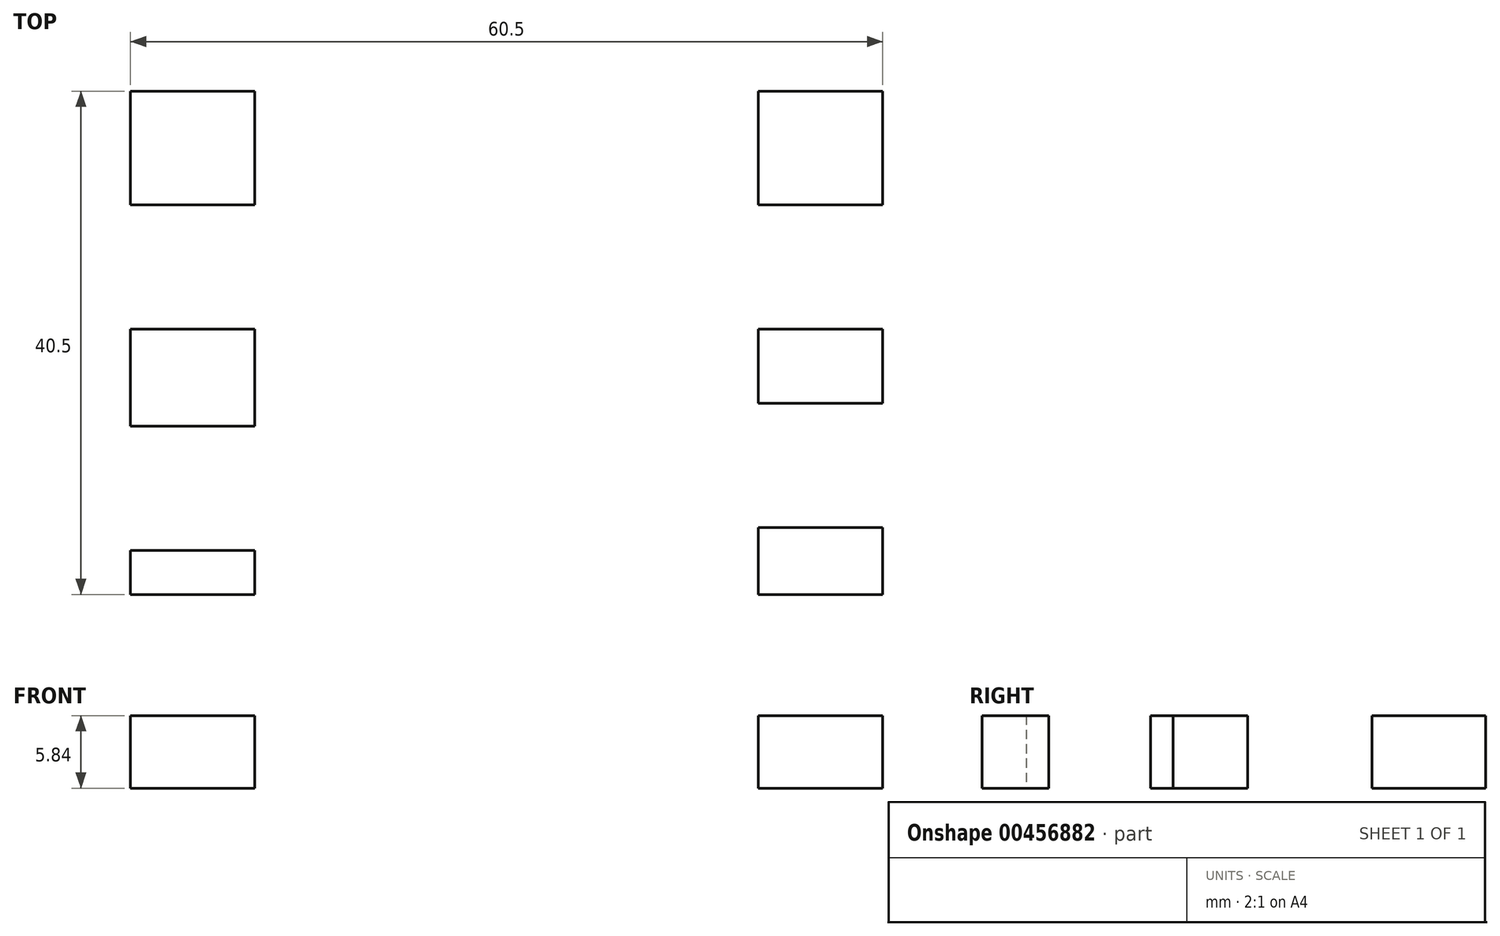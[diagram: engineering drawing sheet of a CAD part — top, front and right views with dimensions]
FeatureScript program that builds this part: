
annotation { "Feature Type Name" : "Feature", "Feature Type Description" : "" }
export const myFeature = defineFeature(function(context is Context, id is Id, definition is map)
    precondition{}
    {
        {
            var Q0;
            Q0=qCreatedBy(makeId("Top.planeOp"),FACE);
            var sketch = newSketch(context, id + "F0", { "sketchPlane" : qUnion([Q0])});
            skLineSegment(sketch, "E0.bottom", {"start": v(-20.25, 20.25) * mm, "end": v(20.25, 20.25) * mm});
            skLineSegment(sketch, "E0.top", {"start": v(-20.25, -20.25) * mm, "end": v(20.25, -20.25) * mm});
            skLineSegment(sketch, "E0.left", {"start": v(-20.25, 20.25) * mm, "end": v(-20.25, -20.25) * mm});
            skLineSegment(sketch, "E0.right", {"start": v(20.25, 20.25) * mm, "end": v(20.25, -20.25) * mm});
            skPoint(sketch, "E1", {"position": v(-20.25, 20.25) * mm});
            skPoint(sketch, "E2", {"position": v(0, 20.25) * mm});
            skPoint(sketch, "E3", {"position": v(20.25, 20.25) * mm});
            skLineSegment(sketch, "E4.bottom", {"start": v(-20.25, 11.12) * mm, "end": v(-30.25, 11.12) * mm});
            skLineSegment(sketch, "E4.top", {"start": v(-20.25, 1.12) * mm, "end": v(-30.25, 1.12) * mm});
            skLineSegment(sketch, "E4.left", {"start": v(-20.25, 11.12) * mm, "end": v(-20.25, 1.12) * mm});
            skLineSegment(sketch, "E4.right", {"start": v(-30.25, 11.12) * mm, "end": v(-30.25, 1.12) * mm});
            skLineSegment(sketch, "E5.bottom", {"start": v(-20.25, -6.7) * mm, "end": v(-30.25, -6.7) * mm});
            skLineSegment(sketch, "E5.top", {"start": v(-20.25, -16.7) * mm, "end": v(-30.25, -16.7) * mm});
            skLineSegment(sketch, "E5.left", {"start": v(-20.25, -6.7) * mm, "end": v(-20.25, -16.7) * mm});
            skLineSegment(sketch, "E5.right", {"start": v(-30.25, -6.7) * mm, "end": v(-30.25, -16.7) * mm});
            skLineSegment(sketch, "E6.bottom", {"start": v(20.25, 11.12) * mm, "end": v(30.25, 11.12) * mm});
            skLineSegment(sketch, "E6.top", {"start": v(20.25, 1.12) * mm, "end": v(30.25, 1.12) * mm});
            skLineSegment(sketch, "E6.left", {"start": v(20.25, 11.12) * mm, "end": v(20.25, 1.12) * mm});
            skLineSegment(sketch, "E6.right", {"start": v(30.25, 11.12) * mm, "end": v(30.25, 1.12) * mm});
            skLineSegment(sketch, "E7.bottom", {"start": v(20.25, -4.88) * mm, "end": v(30.25, -4.88) * mm});
            skLineSegment(sketch, "E7.top", {"start": v(20.25, -14.88) * mm, "end": v(30.25, -14.88) * mm});
            skLineSegment(sketch, "E7.left", {"start": v(20.25, -4.88) * mm, "end": v(20.25, -14.88) * mm});
            skLineSegment(sketch, "E7.right", {"start": v(30.25, -4.88) * mm, "end": v(30.25, -14.88) * mm});
            skLineSegment(sketch, "E8.bottom", {"start": v(-30.25, 20.25) * mm, "end": v(30.25, 20.25) * mm});
            skLineSegment(sketch, "E8.top", {"start": v(-30.25, -20.25) * mm, "end": v(30.25, -20.25) * mm});
            skLineSegment(sketch, "E8.left", {"start": v(-30.25, 20.25) * mm, "end": v(-30.25, -20.25) * mm});
            skLineSegment(sketch, "E8.right", {"start": v(30.25, 20.25) * mm, "end": v(30.25, -20.25) * mm});
            skPoint(sketch, "E9", {"position": v(0, -20.25) * mm});
            skPoint(sketch, "E9.positionSnap0", {"position": v(0, -20.25) * mm});
            skSolve(sketch);
        }
        {
            var Q0;
            {var subQ3=sQuery(id+"F0.wireOp",EDGE,"E4.bottom");Q0=makeQuery(id+"F0.imprint","IMPRINT",FACE,{"disambiguationData":[TD([[makeQuery(id+"F0.imprint","IMPRINT",EDGE,{"derivedFrom":subQ3}),-1.0]])]});}
            var Q1;
            {var subQ3=sQuery(id+"F0.wireOp",EDGE,"E5.top");Q1=makeQuery(id+"F0.imprint","IMPRINT",FACE,{"disambiguationData":[TD([[makeQuery(id+"F0.imprint","IMPRINT",EDGE,{"derivedFrom":subQ3}),1.0]])]});}
            var Q2;
            {var subQ3=sQuery(id+"F0.wireOp",EDGE,"E6.bottom");Q2=makeQuery(id+"F0.imprint","IMPRINT",FACE,{"disambiguationData":[TD([[makeQuery(id+"F0.imprint","IMPRINT",EDGE,{"derivedFrom":subQ3}),1.0]])]});}
            var Q3;
            {var subQ3=sQuery(id+"F0.wireOp",EDGE,"E7.top");Q3=makeQuery(id+"F0.imprint","IMPRINT",FACE,{"disambiguationData":[TD([[makeQuery(id+"F0.imprint","IMPRINT",EDGE,{"derivedFrom":subQ3}),-1.0]])]});}
            var Q4;
            {var subQ0=sQuery(id+"F0.wireOp",EDGE,"E4.top");Q4=makeQuery(id+"F0.imprint","IMPRINT",FACE,{"disambiguationData":[TD([[makeQuery(id+"F0.imprint","IMPRINT",EDGE,{"derivedFrom":subQ0}),1.0]])]});}
            var Q5;
            {var subQ0=sQuery(id+"F0.wireOp",EDGE,"E6.top");Q5=makeQuery(id+"F0.imprint","IMPRINT",FACE,{"disambiguationData":[TD([[makeQuery(id+"F0.imprint","IMPRINT",EDGE,{"derivedFrom":subQ0}),-1.0]])]});}
            var Q6;
            {var subQ1=sQuery(id+"F0.wireOp",EDGE,"E4.left");Q6=makeQuery(id+"F0.imprint","IMPRINT",FACE,{"disambiguationData":[TD([[makeQuery(id+"F0.imprint","IMPRINT",EDGE,{"derivedFrom":subQ1}),1.0]])]});}
            extrude(context, id + "F1", {"entities" : qUnion([Q0, Q1, Q2, Q3, Q4, Q5, Q6]), "depth" : 5.84 * mm});
        }
    });
